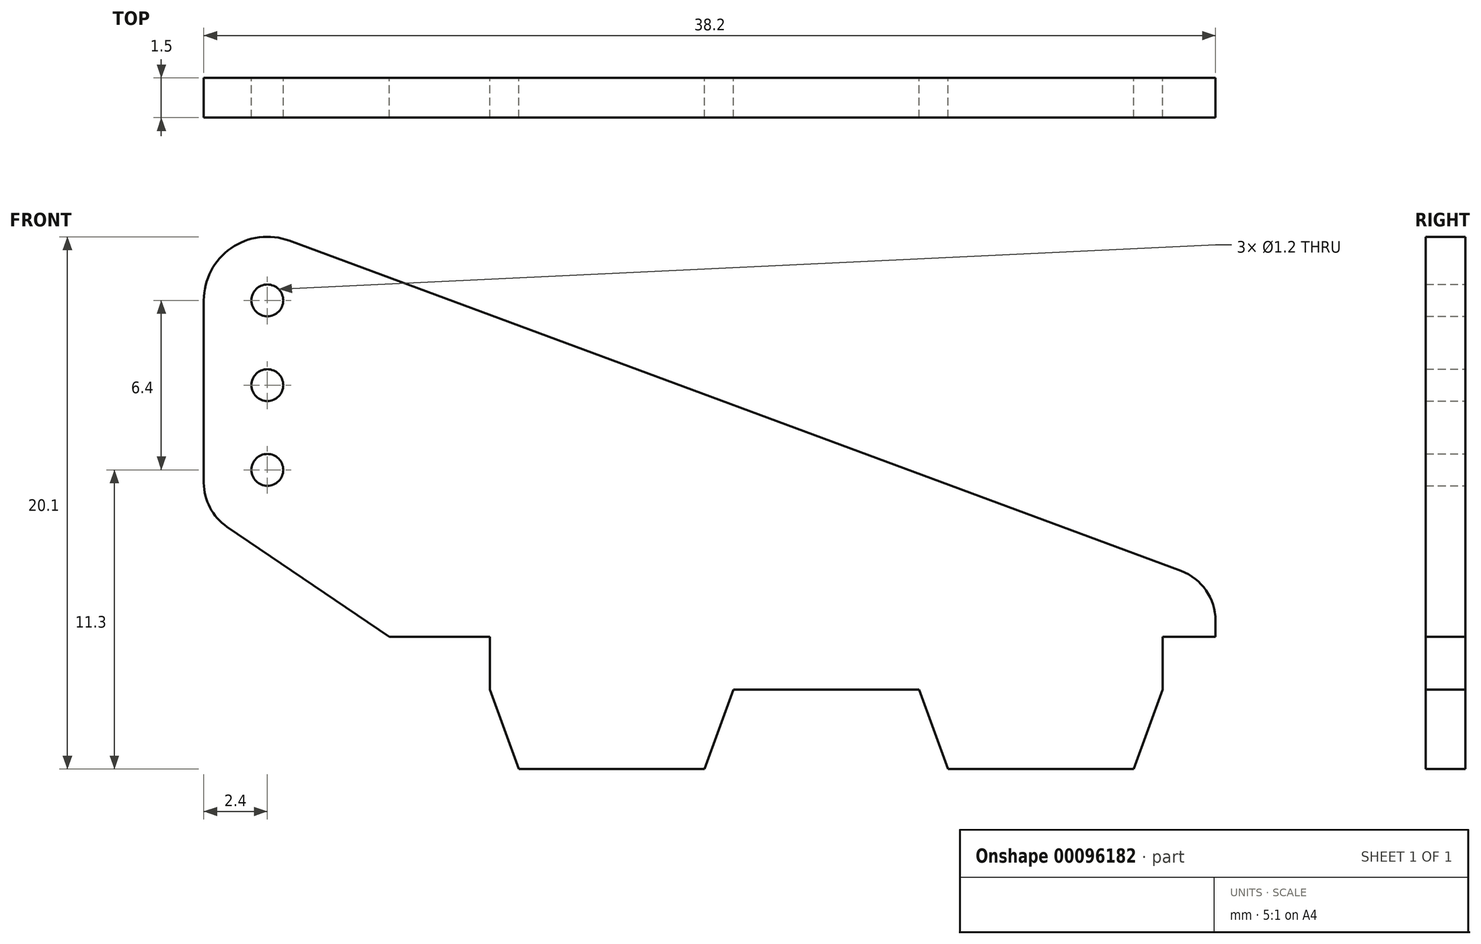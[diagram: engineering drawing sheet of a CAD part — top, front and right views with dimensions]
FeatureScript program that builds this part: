
annotation { "Feature Type Name" : "Feature", "Feature Type Description" : "" }
export const myFeature = defineFeature(function(context is Context, id is Id, definition is map)
    precondition{}
    {
        {
            var Q0;
            Q0=qCreatedBy(makeId("Front.planeOp"),FACE);
            var sketch = newSketch(context, id + "F0", { "sketchPlane" : qUnion([Q0])});
            skLineSegment(sketch, "E0", {"start": v(0, 0) * mm, "end": v(3.8, 0) * mm});
            skLineSegment(sketch, "E1", {"start": v(3.8, 0) * mm, "end": v(3.8, -2) * mm});
            skLineSegment(sketch, "E2", {"start": v(3.8, -2) * mm, "end": v(4.9, -5) * mm});
            skLineSegment(sketch, "E3", {"start": v(4.9, -5) * mm, "end": v(11.9, -5) * mm});
            skLineSegment(sketch, "E4", {"start": v(11.9, -5) * mm, "end": v(13, -2) * mm});
            skLineSegment(sketch, "E5", {"start": v(13, -2) * mm, "end": v(20, -2) * mm});
            skLineSegment(sketch, "E6", {"start": v(20, -2) * mm, "end": v(21.1, -5) * mm});
            skLineSegment(sketch, "E7", {"start": v(21.1, -5) * mm, "end": v(28.1, -5) * mm});
            skLineSegment(sketch, "E8", {"start": v(28.1, -5) * mm, "end": v(29.2, -2) * mm});
            skLineSegment(sketch, "E9", {"start": v(29.2, -2) * mm, "end": v(29.2, 0) * mm});
            skLineSegment(sketch, "E10", {"start": v(29.2, 0) * mm, "end": v(31.2, 0) * mm});
            skLineSegment(sketch, "E11", {"start": v(31.2, 0) * mm, "end": v(31.2, 0.6) * mm});
            skLineSegment(sketch, "E12", {"start": v(29.9, 2.48) * mm, "end": v(-3.77, 14.95) * mm});
            skLineSegment(sketch, "E13", {"start": v(0, 0) * mm, "end": v(-6.12, 4.15) * mm});
            skLineSegment(sketch, "E14", {"start": v(-7, 5.8) * mm, "end": v(-7, 12.7) * mm});
            skArc(sketch, "E15", {"start": v(-7, 12.7) * mm, "mid": v(-5.97, 14.67) * mm, "end": v(-3.77, 14.95) * mm});
            skCircle(sketch, "E16", {"center": v(-4.6, 12.7) * mm, "radius": 0.6 * mm});
            skPoint(sketch, "E17.visualSharp", {"position": v(31.2, 2) * mm});
            skArc(sketch, "E17.filletArc", {"start": v(31.2, 0.6) * mm, "mid": v(30.84, 1.75) * mm, "end": v(29.9, 2.48) * mm});
            skPoint(sketch, "E18.visualSharp", {"position": v(-7, 4.75) * mm});
            skArc(sketch, "E18.filletArc", {"start": v(-7, 5.8) * mm, "mid": v(-6.77, 4.87) * mm, "end": v(-6.12, 4.15) * mm});
            skCircle(sketch, "E19.0.1.0", {"center": v(-4.6, 9.5) * mm, "radius": 0.6 * mm});
            skCircle(sketch, "E19.0.2.0", {"center": v(-4.6, 6.3) * mm, "radius": 0.6 * mm});
            skLineSegment(sketch, "E19.direction1", {"start": v(-4.6, 12.7) * mm, "end": v(-29.6, 12.7) * mm, "construction": true});
            skLineSegment(sketch, "E19.direction2", {"start": v(-4.6, 12.7) * mm, "end": v(-4.6, 9.5) * mm, "construction": true});
            skSolve(sketch);
        }
        {
            var Q0;
            Q0=makeQuery(id+"F0.imprint","IMPRINT",FACE,{"disambiguationData":[TD([[makeQuery(id+"F0.imprint","IMPRINT",EDGE,{"derivedFrom":sQuery(id+"F0.wireOp",EDGE,"E0")}),1.0]])]});
            extrude(context, id + "F1", {"entities" : qUnion([Q0]), "depth" : 1.5 * mm});
        }
    });
